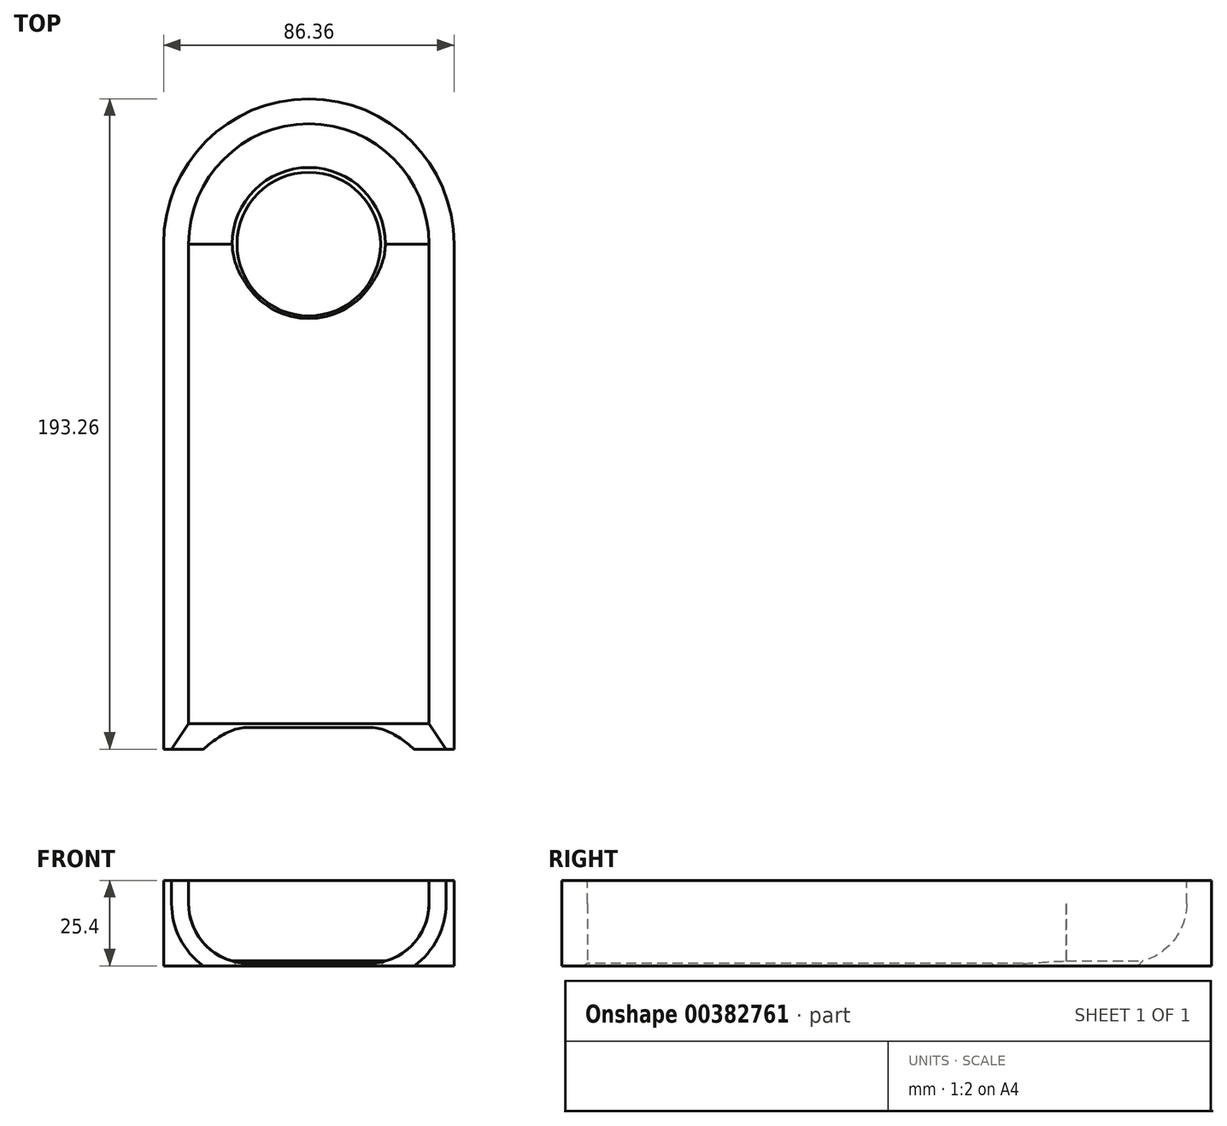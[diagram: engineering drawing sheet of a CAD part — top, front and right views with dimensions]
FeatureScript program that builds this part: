
annotation { "Feature Type Name" : "Feature", "Feature Type Description" : "" }
export const myFeature = defineFeature(function(context is Context, id is Id, definition is map)
    precondition{}
    {
        {
            var Q0;
            Q0=qCreatedBy(makeId("Top.planeOp"),FACE);
            var sketch = newSketch(context, id + "F0", { "sketchPlane" : qUnion([Q0])});
            skCircle(sketch, "E0", {"center": v(0, 0) * mm, "radius": 43.18 * mm});
            skLineSegment(sketch, "E1.bottom", {"start": v(43.18, 0) * mm, "end": v(-43.18, 0) * mm});
            skLineSegment(sketch, "E1.top", {"start": v(43.18, -150.08) * mm, "end": v(-43.18, -150.08) * mm});
            skLineSegment(sketch, "E1.left", {"start": v(43.18, 0) * mm, "end": v(43.18, -150.08) * mm});
            skLineSegment(sketch, "E1.right", {"start": v(-43.18, 0) * mm, "end": v(-43.18, -150.08) * mm});
            skPoint(sketch, "E1.middle", {"position": v(0, -75.04) * mm});
            skSolve(sketch);
        }
        {
            var Q0;
            Q0=makeQuery(id+"F0.imprint","IMPRINT",FACE,{"disambiguationData":[TD([[makeQuery(id+"F0.imprint","IMPRINT",EDGE,{"derivedFrom":sQuery(id+"F0.wireOp",EDGE,"E0")}),1.0]])]});
            extrude(context, id + "F1", {"entities" : qUnion([Q0]), "depth" : 25.4 * mm});
        }
        {
            var Q0;
            Q0=makeQuery(id+"F0.imprint","IMPRINT",FACE,{"disambiguationData":[TD([[makeQuery(id+"F0.imprint","IMPRINT",EDGE,{"derivedFrom":sQuery(id+"F0.wireOp",EDGE,"E0")}),1.0]])]});
            var sketch = newSketch(context, id + "F2", { "sketchPlane" : qUnion([Q0])});
            skCircle(sketch, "E2", {"center": v(0, 0) * mm, "radius": 17.02 * mm});
            skSolve(sketch);
        }
        {
            var Q0;
            Q0=qSketchRegion(id+"F2",true);
            extrude(context, id + "F3", {"entities" : qUnion([Q0]), "operationType" : NewBodyOperationType.REMOVE, "depth" : 27.7 * mm});
        }
        {
            var Q0;
            Q0=makeQuery(id+"F1.opExtrude","CAP_FACE",FACE,{"disambiguationData":[OSD([sQuery(id+"F0.wireOp",EDGE,"E0")])],"isStart":false});
            var sketch = newSketch(context, id + "F4", { "sketchPlane" : qUnion([Q0])});
            skCircle(sketch, "E3", {"center": v(0, 0) * mm, "radius": 35.74 * mm});
            skSolve(sketch);
        }
        {
            var Q0;
            Q0=qSketchRegion(id+"F4",true);
            extrude(context, id + "F5", {"entities" : qUnion([Q0]), "operationType" : NewBodyOperationType.REMOVE, "oppositeDirection" : true, "depth" : 24.64 * mm});
        }
        {
            var Q0;
            Q0=makeQuery(id+"F5.boolean.opBoolean","COPY",EDGE,{"derivedFrom":makeQuery(id+"F5.opExtrude","CAP_EDGE",EDGE,{"disambiguationData":[OSD([sQuery(id+"F4.wireOp",EDGE,"E3")])],"isStart":false})});
            fillet(context, id + "F6", {"entities" : qUnion([Q0]), "radius" : 17.78 * mm, "allowEdgeOverflow" : false});
        }
        {
            var Q0;
            Q0=makeQuery(id+"F0.imprint","IMPRINT",FACE,{"disambiguationData":[TD([[makeQuery(id+"F0.imprint","IMPRINT",EDGE,{"derivedFrom":sQuery(id+"F0.wireOp",EDGE,"E1.top")}),-1.0]])]});
            extrude(context, id + "F7", {"entities" : qUnion([Q0]), "operationType" : NewBodyOperationType.ADD, "depth" : 25.4 * mm});
        }
        {
            var Q0;
            {var subQ0=sQuery(id+"F0.wireOp",EDGE,"E0");Q0=makeQuery(id+"F7.boolean.opBoolean","MERGE",FACE,{"derivedFrom":[makeQuery(id+"F1.opExtrude","CAP_FACE",FACE,{"disambiguationData":[OSD([subQ0])],"isStart":false}),makeQuery(id+"F7.opExtrude","CAP_FACE",FACE,{"disambiguationData":[OSD([subQ0,sQuery(id+"F0.wireOp",EDGE,"E1.top"),sQuery(id+"F0.wireOp",EDGE,"E1.left"),sQuery(id+"F0.wireOp",EDGE,"E1.right")])],"isStart":false})]});}
            var sketch = newSketch(context, id + "F8", { "sketchPlane" : qUnion([Q0])});
            skLineSegment(sketch, "E4.bottom", {"start": v(35.74, 0) * mm, "end": v(-35.74, 0) * mm});
            skLineSegment(sketch, "E4.top", {"start": v(35.74, -155.25) * mm, "end": v(-35.74, -155.25) * mm});
            skLineSegment(sketch, "E4.left", {"start": v(35.74, 0) * mm, "end": v(35.74, -155.25) * mm});
            skLineSegment(sketch, "E4.right", {"start": v(-35.74, 0) * mm, "end": v(-35.74, -155.25) * mm});
            skPoint(sketch, "E4.middle", {"position": v(0, -77.62) * mm});
            skSolve(sketch);
        }
        {
            var Q0;
            Q0 = qSketchRegion(id + "F8", true);
            extrude(context, id + "F9", {"entities" : qUnion([Q0]), "operationType" : NewBodyOperationType.REMOVE, "oppositeDirection" : true, "depth" : 24.64 * mm});
        }
        {
            var Q0;
            Q0=makeQuery(id+"F9.boolean.opBoolean","COPY",EDGE,{"derivedFrom":makeQuery(id+"F9.opExtrude","CAP_EDGE",EDGE,{"disambiguationData":[OSD([sQuery(id+"F8.wireOp",EDGE,"E4.left")])],"isStart":false})});
            var Q1;
            Q1=makeQuery(id+"F9.boolean.opBoolean","COPY",EDGE,{"derivedFrom":makeQuery(id+"F9.opExtrude","CAP_EDGE",EDGE,{"disambiguationData":[OSD([sQuery(id+"F8.wireOp",EDGE,"E4.right")])],"isStart":false})});
            fillet(context, id + "F10", {"entities" : qUnion([Q0, Q1]), "radius" : 17.78 * mm, "tangentPropagation" : true, "allowEdgeOverflow" : false});
        }
        {
            var Q0;
            Q0=makeQuery(id+"F5.boolean.opBoolean","INTERSECT",EDGE,{"derivedFrom":[makeQuery(id+"F3.boolean.opBoolean","COPY",FACE,{"derivedFrom":makeQuery(id+"F3.opExtrude","SWEPT_FACE",FACE,{"disambiguationData":[OSD([sQuery(id+"F2.wireOp",EDGE,"E2")])]})}),makeQuery(id+"F5.opExtrude","CAP_FACE",FACE,{"disambiguationData":[OSD([sQuery(id+"F4.wireOp",EDGE,"E3")])],"isStart":false})]});
            chamfer(context, id + "F11", {"entities" : qUnion([Q0]), "width" : 5.08 * mm, "tangentPropagation" : true});
        }
        {
            var Q0;
            Q0=makeQuery(id+"F9.boolean.opBoolean","INTERSECT",EDGE,{"derivedFrom":[makeQuery(id+"F7.opExtrude","SWEPT_FACE",FACE,{"disambiguationData":[OSD([sQuery(id+"F0.wireOp",EDGE,"E1.top")])]}),makeQuery(id+"F9.opExtrude","CAP_FACE",FACE,{"disambiguationData":[OSD([sQuery(id+"F8.wireOp",EDGE,"E4.bottom"),sQuery(id+"F8.wireOp",EDGE,"E4.top"),sQuery(id+"F8.wireOp",EDGE,"E4.left"),sQuery(id+"F8.wireOp",EDGE,"E4.right")])],"isStart":false})]});
            chamfer(context, id + "F12", {"entities" : qUnion([Q0]), "chamferType" : ChamferType.TWO_OFFSETS, "width1" : 5.08 * mm, "oppositeDirection" : false, "width2" : 7.62 * mm, "tangentPropagation" : true});
        }
    });
